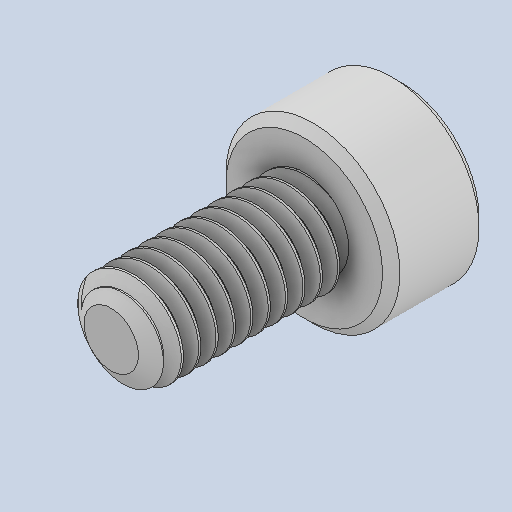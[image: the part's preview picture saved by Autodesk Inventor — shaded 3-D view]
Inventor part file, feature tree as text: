
AUTODESK INVENTOR PART (.ipt)
format: ipt  version: 2023 (Build 270158000, 158)  size: 511,488 bytes
history: native  units: mm
features: chamfer x1
ambient origin geometry x8: Origin, YZ Plane, XZ Plane, XY Plane, X Axis, Y Axis, Z Axis, Center Point
bodies: Solid1 (feature_tree)
feature tree (1):
  chamfer  "Chamfer1"  [1 undecoded]
note: 1 required parameter value undecoded (feature->parameter linkage not recoverable at this tier; creation-order binding heuristic only, values carry confidence <= 0.55)
